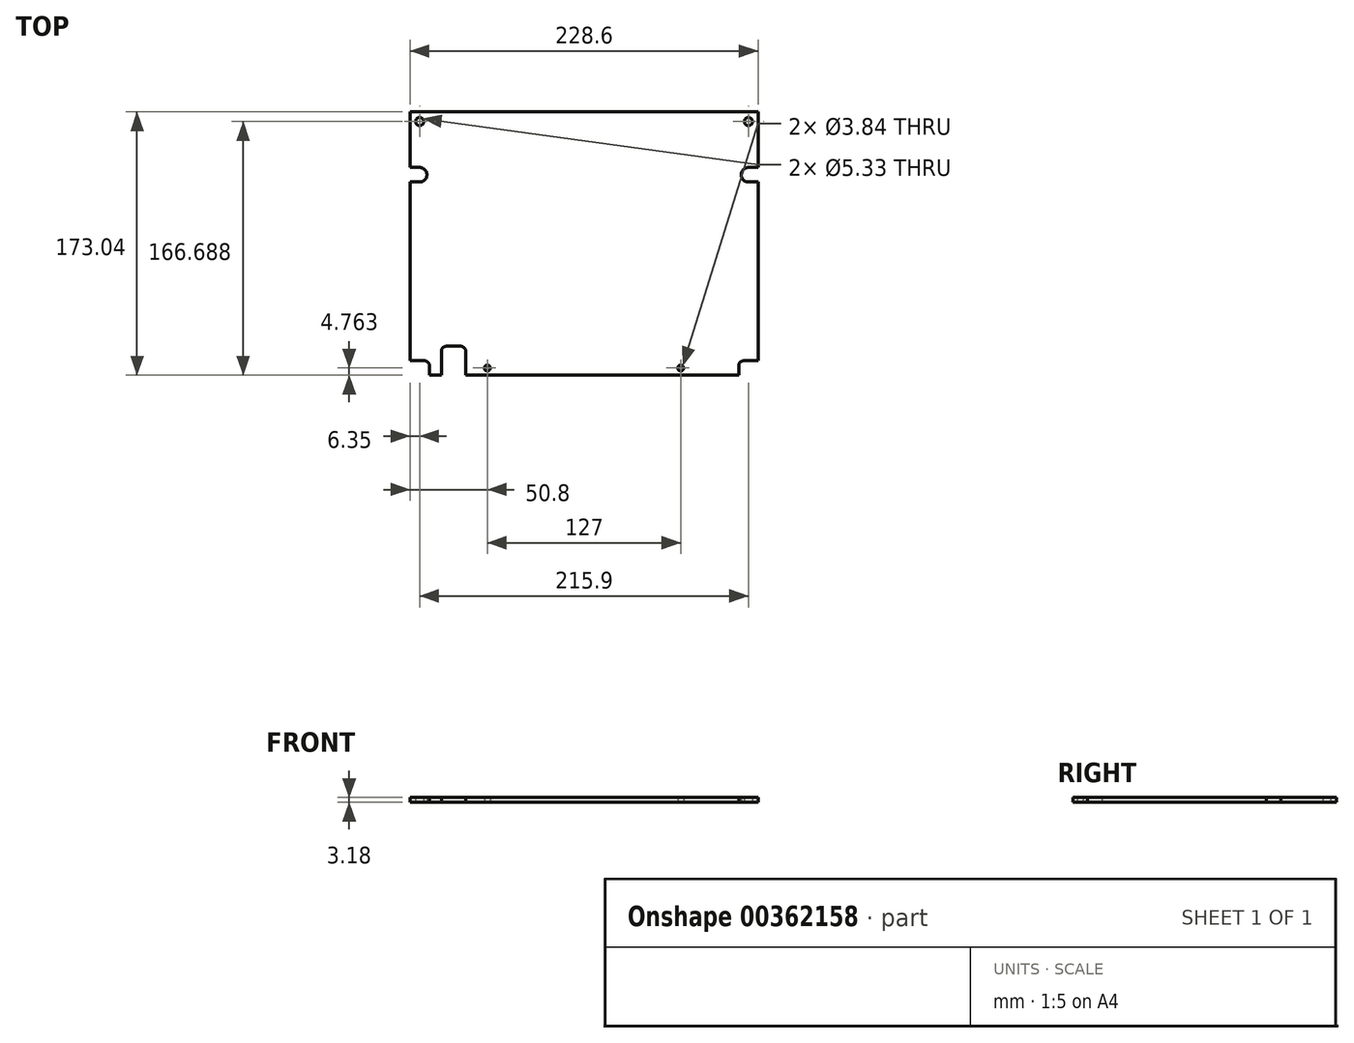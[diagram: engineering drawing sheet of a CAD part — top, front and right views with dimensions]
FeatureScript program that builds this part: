
annotation { "Feature Type Name" : "Feature", "Feature Type Description" : "" }
export const myFeature = defineFeature(function(context is Context, id is Id, definition is map)
    precondition{}
    {
        {
            var Q0;
            Q0=qCreatedBy(makeId("Top.planeOp"),FACE);
            var sketch = newSketch(context, id + "F0", { "sketchPlane" : qUnion([Q0])});
            skLineSegment(sketch, "E0.bottom", {"start": v(12.7, 0) * mm, "end": v(20.64, 0) * mm});
            skLineSegment(sketch, "E0.top", {"start": v(0, 127) * mm, "end": v(6.35, 127) * mm});
            skLineSegment(sketch, "E0.left", {"start": v(0, 9.52) * mm, "end": v(0, 127) * mm});
            skLineSegment(sketch, "E0.right", {"start": v(228.6, 9.53) * mm, "end": v(228.6, 127) * mm});
            skLineSegment(sketch, "E1", {"start": v(0, 136.53) * mm, "end": v(0, 173.04) * mm});
            skLineSegment(sketch, "E2", {"start": v(0, 173.04) * mm, "end": v(228.6, 173.04) * mm});
            skLineSegment(sketch, "E3", {"start": v(228.6, 173.04) * mm, "end": v(228.6, 136.52) * mm});
            skLineSegment(sketch, "E4", {"start": v(0, 136.53) * mm, "end": v(6.35, 136.53) * mm});
            skLineSegment(sketch, "E5", {"start": v(228.6, 136.52) * mm, "end": v(222.25, 136.52) * mm});
            skArc(sketch, "E6", {"start": v(222.25, 136.53) * mm, "mid": v(217.49, 131.76) * mm, "end": v(222.25, 127) * mm});
            skArc(sketch, "E7", {"start": v(6.35, 127) * mm, "mid": v(11.11, 131.76) * mm, "end": v(6.35, 136.53) * mm});
            skLineSegment(sketch, "E8", {"start": v(0, 173.04) * mm, "end": v(0, 208.79) * mm, "construction": true});
            skLineSegment(sketch, "E9", {"start": v(0, 208.79) * mm, "end": v(228.6, 208.79) * mm, "construction": true});
            skLineSegment(sketch, "E10", {"start": v(228.6, 173.04) * mm, "end": v(228.6, 208.79) * mm, "construction": true});
            skLineSegment(sketch, "E11.trimOffspring", {"start": v(222.25, 127) * mm, "end": v(228.6, 127) * mm});
            skLineSegment(sketch, "E12", {"start": v(6.35, 127) * mm, "end": v(222.25, 127) * mm, "construction": true});
            skLineSegment(sketch, "E13", {"start": v(12.7, 9.53) * mm, "end": v(0, 9.52) * mm});
            skLineSegment(sketch, "E14", {"start": v(12.7, 9.53) * mm, "end": v(12.7, 0) * mm});
            skLineSegment(sketch, "E15", {"start": v(215.9, 0) * mm, "end": v(215.9, 9.53) * mm});
            skLineSegment(sketch, "E16", {"start": v(215.9, 9.53) * mm, "end": v(228.6, 9.53) * mm});
            skLineSegment(sketch, "E17", {"start": v(20.64, 0) * mm, "end": v(20.64, 19.05) * mm});
            skLineSegment(sketch, "E18", {"start": v(20.64, 19.05) * mm, "end": v(36.51, 19.05) * mm});
            skLineSegment(sketch, "E19", {"start": v(36.51, 19.05) * mm, "end": v(36.51, 0) * mm});
            skLineSegment(sketch, "E20.trimOffspring", {"start": v(36.51, 0) * mm, "end": v(215.9, 0) * mm});
            skLineSegment(sketch, "E21", {"start": v(36.51, 0) * mm, "end": v(20.64, 0) * mm, "construction": true});
            skLineSegment(sketch, "E22", {"start": v(50.8, 4.76) * mm, "end": v(177.8, 4.76) * mm, "construction": true});
            skPoint(sketch, "E23", {"position": v(50.8, 4.76) * mm});
            skPoint(sketch, "E24", {"position": v(177.8, 4.76) * mm});
            skLineSegment(sketch, "E25", {"start": v(50.8, 4.76) * mm, "end": v(36.51, 4.76) * mm, "construction": true});
            skLineSegment(sketch, "E26", {"start": v(177.8, 4.76) * mm, "end": v(215.9, 4.76) * mm, "construction": true});
            skLineSegment(sketch, "E27", {"start": v(6.35, 173.04) * mm, "end": v(6.35, 166.69) * mm, "construction": true});
            skLineSegment(sketch, "E28", {"start": v(6.35, 166.69) * mm, "end": v(0, 166.69) * mm, "construction": true});
            skPoint(sketch, "E29", {"position": v(6.35, 166.69) * mm});
            skLineSegment(sketch, "E30", {"start": v(222.25, 173.04) * mm, "end": v(222.25, 166.69) * mm, "construction": true});
            skLineSegment(sketch, "E31", {"start": v(222.25, 166.69) * mm, "end": v(228.6, 166.69) * mm, "construction": true});
            skPoint(sketch, "E32", {"position": v(222.25, 166.69) * mm});
            skSolve(sketch);
        }
        {
            var Q0;
            Q0=makeQuery(id+"F0.imprint","IMPRINT",FACE,{"disambiguationData":[TD([[makeQuery(id+"F0.imprint","IMPRINT",EDGE,{"derivedFrom":sQuery(id+"F0.wireOp",EDGE,"E0.bottom")}),1.0]])]});
            extrude(context, id + "F1", {"entities" : qUnion([Q0]), "depth" : 3.17 * mm});
        }
        {
            var Q0;
            Q0=sQuery(id+"F0.wireOp",VERTEX,"E23");
            var Q1;
            Q1=sQuery(id+"F0.wireOp",VERTEX,"E24");
            var Q2;
            Q2=makeQuery(id+"F1.opExtrude","SWEPT_BODY",BODY,{"disambiguationData":[OSD([sQuery(id+"F0.wireOp",EDGE,"E0.bottom"),sQuery(id+"F0.wireOp",EDGE,"E0.top"),sQuery(id+"F0.wireOp",EDGE,"E0.left"),sQuery(id+"F0.wireOp",EDGE,"E0.right"),sQuery(id+"F0.wireOp",EDGE,"E1"),sQuery(id+"F0.wireOp",EDGE,"E2"),sQuery(id+"F0.wireOp",EDGE,"E3"),sQuery(id+"F0.wireOp",EDGE,"E4"),sQuery(id+"F0.wireOp",EDGE,"E5"),sQuery(id+"F0.wireOp",EDGE,"E6"),sQuery(id+"F0.wireOp",EDGE,"E7"),sQuery(id+"F0.wireOp",EDGE,"E11.trimOffspring"),sQuery(id+"F0.wireOp",EDGE,"E13"),sQuery(id+"F0.wireOp",EDGE,"E14"),sQuery(id+"F0.wireOp",EDGE,"E15"),sQuery(id+"F0.wireOp",EDGE,"E16"),sQuery(id+"F0.wireOp",EDGE,"E17"),sQuery(id+"F0.wireOp",EDGE,"E18"),sQuery(id+"F0.wireOp",EDGE,"E19"),sQuery(id+"F0.wireOp",EDGE,"E20.trimOffspring")])]});
            hole(context, id + "F2", {"style" : HoleStyle.SIMPLE, "endStyle" : HoleEndStyle.THROUGH, "oppositeDirection" : true, "holeDiameter" : 3.84 * mm, "isTappedThrough" : true, "tappedDepth" : 12.7 * mm, "tapClearance" : 3, "startFromSketch" : true, "locations" : qUnion([Q0, Q1]), "scope" : qUnion([Q2])});
        }
        {
            var Q0;
            Q0=sQuery(id+"F0.wireOp",VERTEX,"E29");
            var Q1;
            Q1=sQuery(id+"F0.wireOp",VERTEX,"E32");
            var Q2;
            Q2=makeQuery(id+"F1.opExtrude","SWEPT_BODY",BODY,{"disambiguationData":[OSD([sQuery(id+"F0.wireOp",EDGE,"E0.bottom"),sQuery(id+"F0.wireOp",EDGE,"E0.top"),sQuery(id+"F0.wireOp",EDGE,"E0.left"),sQuery(id+"F0.wireOp",EDGE,"E0.right"),sQuery(id+"F0.wireOp",EDGE,"E1"),sQuery(id+"F0.wireOp",EDGE,"E2"),sQuery(id+"F0.wireOp",EDGE,"E3"),sQuery(id+"F0.wireOp",EDGE,"E4"),sQuery(id+"F0.wireOp",EDGE,"E5"),sQuery(id+"F0.wireOp",EDGE,"E6"),sQuery(id+"F0.wireOp",EDGE,"E7"),sQuery(id+"F0.wireOp",EDGE,"E11.trimOffspring"),sQuery(id+"F0.wireOp",EDGE,"E13"),sQuery(id+"F0.wireOp",EDGE,"E14"),sQuery(id+"F0.wireOp",EDGE,"E15"),sQuery(id+"F0.wireOp",EDGE,"E16"),sQuery(id+"F0.wireOp",EDGE,"E17"),sQuery(id+"F0.wireOp",EDGE,"E18"),sQuery(id+"F0.wireOp",EDGE,"E19"),sQuery(id+"F0.wireOp",EDGE,"E20.trimOffspring")])]});
            hole(context, id + "F3", {"style" : HoleStyle.SIMPLE, "endStyle" : HoleEndStyle.THROUGH, "oppositeDirection" : true, "holeDiameter" : 5.33 * mm, "isTappedThrough" : true, "tappedDepth" : 12.7 * mm, "tapClearance" : 3, "startFromSketch" : true, "locations" : qUnion([Q0, Q1]), "scope" : qUnion([Q2])});
        }
        {
            var Q0;
            Q0=makeQuery(id+"F1.opExtrude","SWEPT_EDGE",EDGE,{"disambiguationData":[OSD([sQuery(id+"F0.wireOp",EDGE,"E15"),sQuery(id+"F0.wireOp",EDGE,"E16")])]});
            var Q1;
            Q1=makeQuery(id+"F1.opExtrude","SWEPT_EDGE",EDGE,{"disambiguationData":[OSD([sQuery(id+"F0.wireOp",EDGE,"E13"),sQuery(id+"F0.wireOp",EDGE,"E14")])]});
            var Q2;
            Q2=makeQuery(id+"F1.opExtrude","SWEPT_EDGE",EDGE,{"disambiguationData":[OSD([sQuery(id+"F0.wireOp",EDGE,"E18"),sQuery(id+"F0.wireOp",EDGE,"E19")])]});
            var Q3;
            Q3=makeQuery(id+"F1.opExtrude","SWEPT_EDGE",EDGE,{"disambiguationData":[OSD([sQuery(id+"F0.wireOp",EDGE,"E17"),sQuery(id+"F0.wireOp",EDGE,"E18")])]});
            fillet(context, id + "F4", {"entities" : qUnion([Q0, Q1, Q2, Q3]), "radius" : 3.17 * mm, "tangentPropagation" : true, "allowEdgeOverflow" : false});
        }
    });
